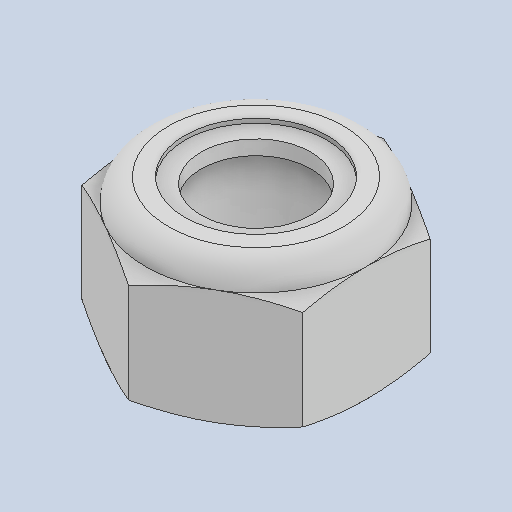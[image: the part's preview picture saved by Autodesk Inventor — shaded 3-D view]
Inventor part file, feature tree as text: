
AUTODESK INVENTOR PART (.ipt)
format: ipt  version: 2023 (Build 270158030, 158C)  size: 193,024 bytes
history: native  units: in
note: dims shown in document units (in); Inventor stores cm internally (conversion verified against a paired STEP export)
features: other x1, revolve x1
ambient origin geometry x8: Origin, YZ Plane, XZ Plane, XY Plane, X Axis, Y Axis, Z Axis, Center Point
bodies: Solid1 (feature_tree), Solid2 (feature_tree)
feature tree (2):
  other  "Cut-Revolve4"
  revolve  "Revolve2"  [1 undecoded]
note: 1 required parameter value undecoded (feature->parameter linkage not recoverable at this tier; creation-order binding heuristic only, values carry confidence <= 0.55)
